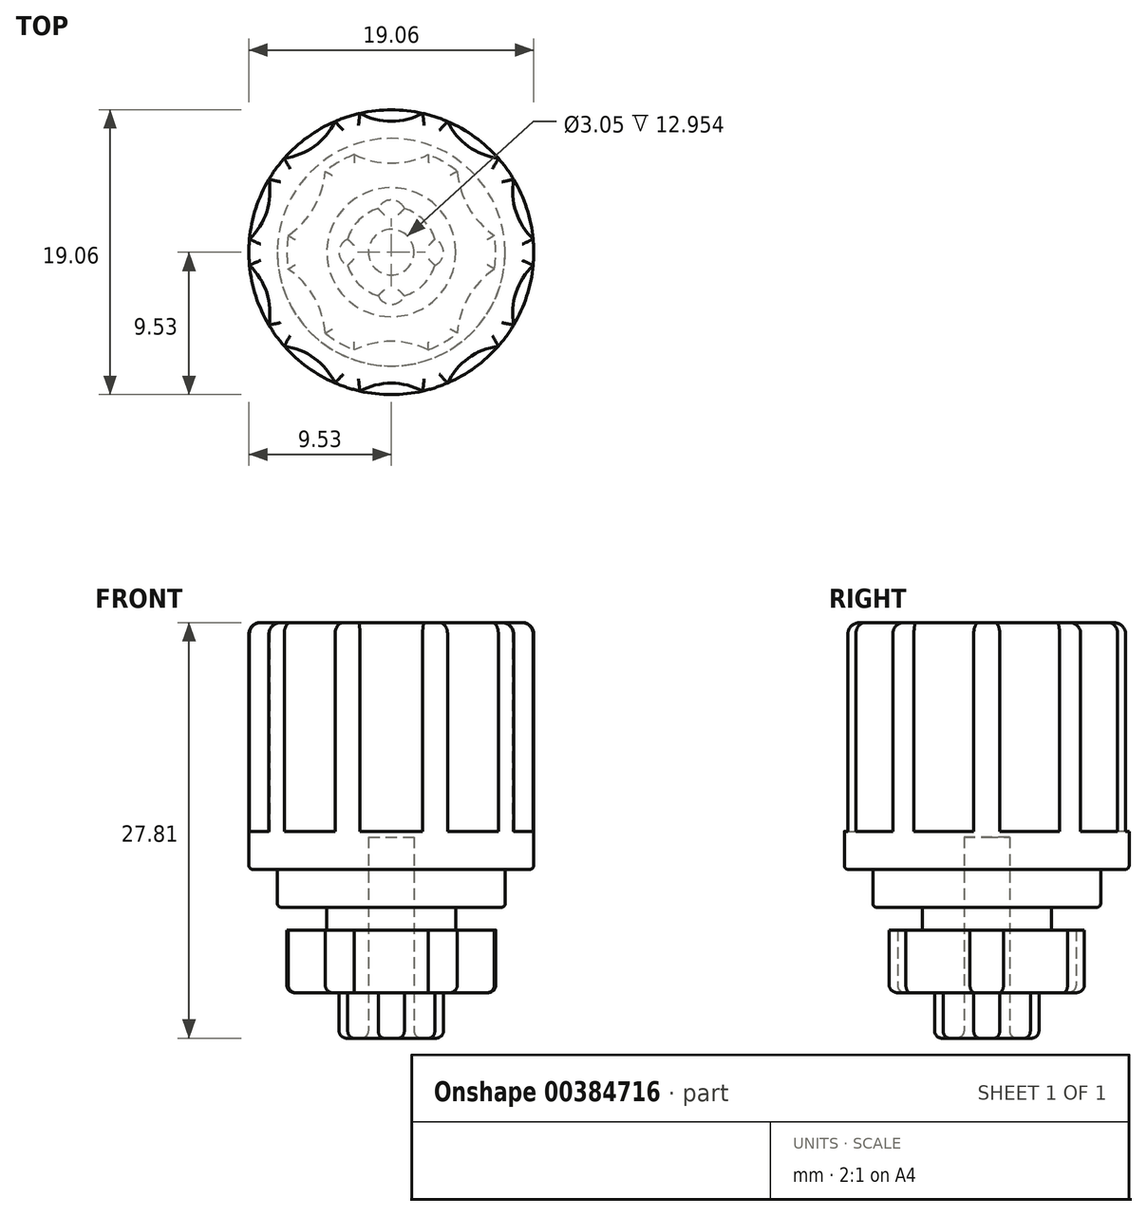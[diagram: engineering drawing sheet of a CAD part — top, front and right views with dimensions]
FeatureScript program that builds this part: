
annotation { "Feature Type Name" : "Feature", "Feature Type Description" : "" }
export const myFeature = defineFeature(function(context is Context, id is Id, definition is map)
    precondition{}
    {
        {
            var Q0;
            Q0=qCreatedBy(makeId("Top.planeOp"),FACE);
            var sketch = newSketch(context, id + "F0", { "sketchPlane" : qUnion([Q0])});
            skCircle(sketch, "E0", {"center": v(0, 0) * mm, "radius": 9.53 * mm});
            skSolve(sketch);
        }
        {
            var Q0;
            Q0=qSketchRegion(id+"F0",true);
            extrude(context, id + "F1", {"entities" : qUnion([Q0]), "depth" : 16.5 * mm});
        }
        {
            var Q0;
            Q0=makeQuery(id+"F1.opExtrude","CAP_FACE",FACE,{"disambiguationData":[OSD([sQuery(id+"F0.wireOp",EDGE,"E0")])],"isStart":false});
            var sketch = newSketch(context, id + "F2", { "sketchPlane" : qUnion([Q0])});
            skCircle(sketch, "E1", {"center": v(0, 13.2) * mm, "radius": 4.45 * mm});
            skCircle(sketch, "E2.1.0", {"center": v(-7.76, 10.69) * mm, "radius": 4.45 * mm});
            skCircle(sketch, "E2.2.0", {"center": v(-12.56, 4.08) * mm, "radius": 4.44 * mm});
            skCircle(sketch, "E2.3.0", {"center": v(-12.56, -4.08) * mm, "radius": 4.45 * mm});
            skCircle(sketch, "E2.4.0", {"center": v(-7.76, -10.69) * mm, "radius": 4.44 * mm});
            skCircle(sketch, "E2.5.0", {"center": v(0, -13.2) * mm, "radius": 4.44 * mm});
            skCircle(sketch, "E2.6.0", {"center": v(7.76, -10.69) * mm, "radius": 4.45 * mm});
            skCircle(sketch, "E2.7.0", {"center": v(12.56, -4.08) * mm, "radius": 4.45 * mm});
            skCircle(sketch, "E2.8.0", {"center": v(12.56, 4.08) * mm, "radius": 4.45 * mm});
            skCircle(sketch, "E2.9.0", {"center": v(7.76, 10.69) * mm, "radius": 4.45 * mm});
            skPoint(sketch, "E2.center", {"position": v(0, 0) * mm});
            skSolve(sketch);
        }
        {
            var Q0;
            Q0=qSketchRegion(id+"F2",true);
            extrude(context, id + "F3", {"entities" : qUnion([Q0]), "operationType" : NewBodyOperationType.REMOVE, "oppositeDirection" : true, "depth" : 13.97 * mm});
        }
        {
            var Q0;
            Q0=makeQuery(id+"F1.opExtrude","CAP_FACE",FACE,{"disambiguationData":[OSD([sQuery(id+"F0.wireOp",EDGE,"E0")])],"isStart":false});
            fillet(context, id + "F4", {"entities" : qUnion([Q0]), "radius" : 0.76 * mm, "tangentPropagation" : true, "allowEdgeOverflow" : false});
        }
        {
            var Q0;
            Q0=makeQuery(id+"F1.opExtrude","CAP_FACE",FACE,{"disambiguationData":[OSD([sQuery(id+"F0.wireOp",EDGE,"E0")])],"isStart":true});
            var sketch = newSketch(context, id + "F5", { "sketchPlane" : qUnion([Q0])});
            skCircle(sketch, "E3", {"center": v(0, 0) * mm, "radius": 6.99 * mm});
            skSolve(sketch);
        }
        {
            var Q0;
            Q0=qSketchRegion(id+"F5",true);
            extrude(context, id + "F6", {"entities" : qUnion([Q0]), "operationType" : NewBodyOperationType.ADD, "depth" : 8.25 * mm, "offsetDistance" : 25.4 * mm});
        }
        {
            var Q0;
            Q0=makeQuery(id+"F6.opExtrude","CAP_FACE",FACE,{"disambiguationData":[OSD([sQuery(id+"F5.wireOp",EDGE,"E3")])],"isStart":false});
            var sketch = newSketch(context, id + "F7", { "sketchPlane" : qUnion([Q0])});
            skCircle(sketch, "E4", {"center": v(0, 11.68) * mm, "radius": 5.72 * mm});
            skCircle(sketch, "E5.1.0", {"center": v(-10.12, 5.84) * mm, "radius": 5.72 * mm});
            skCircle(sketch, "E5.2.0", {"center": v(-10.12, -5.84) * mm, "radius": 5.72 * mm});
            skCircle(sketch, "E5.3.0", {"center": v(0, -11.68) * mm, "radius": 5.72 * mm});
            skCircle(sketch, "E5.4.0", {"center": v(10.12, -5.84) * mm, "radius": 5.72 * mm});
            skPoint(sketch, "E5.center", {"position": v(0, 0) * mm});
            skCircle(sketch, "E6.1.5.0", {"center": v(10.12, 5.84) * mm, "radius": 5.72 * mm});
            skSolve(sketch);
        }
        {
            var Q0;
            Q0=qSketchRegion(id+"F7",true);
            extrude(context, id + "F8", {"entities" : qUnion([Q0]), "operationType" : NewBodyOperationType.REMOVE, "oppositeDirection" : true, "depth" : 7.62 * mm});
        }
        {
            var Q0;
            Q0=makeQuery(id+"F8.boolean.opBoolean","MERGE",FACE,{"derivedFrom":[makeQuery(id+"F1.opExtrude","CAP_FACE",FACE,{"disambiguationData":[OSD([sQuery(id+"F0.wireOp",EDGE,"E0")])],"isStart":true}),makeQuery(id+"F8.opExtrude","CAP_FACE",FACE,{"disambiguationData":[OSD([sQuery(id+"F7.wireOp",EDGE,"E4")])],"isStart":false}),makeQuery(id+"F8.opExtrude","CAP_FACE",FACE,{"disambiguationData":[OSD([sQuery(id+"F7.wireOp",EDGE,"E5.1.0")])],"isStart":false}),makeQuery(id+"F8.opExtrude","CAP_FACE",FACE,{"disambiguationData":[OSD([sQuery(id+"F7.wireOp",EDGE,"E5.2.0")])],"isStart":false}),makeQuery(id+"F8.opExtrude","CAP_FACE",FACE,{"disambiguationData":[OSD([sQuery(id+"F7.wireOp",EDGE,"E5.3.0")])],"isStart":false}),makeQuery(id+"F8.opExtrude","CAP_FACE",FACE,{"disambiguationData":[OSD([sQuery(id+"F7.wireOp",EDGE,"E5.4.0")])],"isStart":false})]});
            var sketch = newSketch(context, id + "F9", { "sketchPlane" : qUnion([Q0])});
            skCircle(sketch, "E7", {"center": v(0, 0) * mm, "radius": 6.99 * mm});
            skCircle(sketch, "E8", {"center": v(0, 0) * mm, "radius": 4.32 * mm});
            skSolve(sketch);
        }
        {
            var Q0;
            Q0=qSketchRegion(id+"F9",true);
            extrude(context, id + "F10", {"entities" : qUnion([Q0]), "operationType" : NewBodyOperationType.REMOVE, "depth" : 4.06 * mm, "offsetDistance" : 25.4 * mm});
        }
        {
            var Q0;
            Q0=makeQuery(id+"F10.boolean.opBoolean","MERGE",FACE,{"derivedFrom":[makeQuery(id+"F1.opExtrude","CAP_FACE",FACE,{"disambiguationData":[OSD([sQuery(id+"F0.wireOp",EDGE,"E0")])],"isStart":true}),makeQuery(id+"F10.opExtrude","CAP_FACE",FACE,{"disambiguationData":[OSD([sQuery(id+"F9.wireOp",EDGE,"E7"),sQuery(id+"F9.wireOp",EDGE,"E8")])],"isStart":true})]});
            var sketch = newSketch(context, id + "F11", { "sketchPlane" : qUnion([Q0])});
            skCircle(sketch, "E9", {"center": v(0, 0) * mm, "radius": 7.62 * mm});
            skSolve(sketch);
        }
        {
            var Q0;
            Q0=qSketchRegion(id+"F11",true);
            extrude(context, id + "F12", {"entities" : qUnion([Q0]), "operationType" : NewBodyOperationType.ADD, "depth" : 2.54 * mm, "offsetDistance" : 25.4 * mm});
        }
        {
            var Q0;
            Q0=makeQuery(id+"F6.opExtrude","CAP_FACE",FACE,{"disambiguationData":[OSD([sQuery(id+"F5.wireOp",EDGE,"E3")])],"isStart":false});
            fillet(context, id + "F13", {"entities" : qUnion([Q0]), "radius" : 0.5 * mm, "tangentPropagation" : true, "allowEdgeOverflow" : false});
        }
        {
            var Q0;
            Q0=makeQuery(id+"F12.opExtrude","CAP_EDGE",EDGE,{"disambiguationData":[OSD([sQuery(id+"F11.wireOp",EDGE,"E9")])],"isStart":false});
            var Q1;
            Q1=makeQuery(id+"F1.opExtrude","CAP_EDGE",EDGE,{"disambiguationData":[OSD([sQuery(id+"F0.wireOp",EDGE,"E0")])],"isStart":true});
            var Q2;
            Q2=makeQuery(id+"F3.boolean.opBoolean","INTERSECT",EDGE,{"derivedFrom":[makeQuery(id+"F1.opExtrude","SWEPT_FACE",FACE,{"disambiguationData":[OSD([sQuery(id+"F0.wireOp",EDGE,"E0")])]}),makeQuery(id+"F3.opExtrude","CAP_FACE",FACE,{"disambiguationData":[OSD([sQuery(id+"F2.wireOp",EDGE,"cbdd18e0-91e5-42c7-8da3-7d40650399a5.4.0")])],"isStart":false})]});
            var Q3;
            Q3=makeQuery(id+"F3.boolean.opBoolean","INTERSECT",EDGE,{"derivedFrom":[makeQuery(id+"F1.opExtrude","SWEPT_FACE",FACE,{"disambiguationData":[OSD([sQuery(id+"F0.wireOp",EDGE,"E0")])]}),makeQuery(id+"F3.opExtrude","CAP_FACE",FACE,{"disambiguationData":[OSD([sQuery(id+"F2.wireOp",EDGE,"cbdd18e0-91e5-42c7-8da3-7d40650399a5.5.0")])],"isStart":false})]});
            var Q4;
            Q4=makeQuery(id+"F3.boolean.opBoolean","INTERSECT",EDGE,{"disambiguationData":[OD(0.0)],"derivedFrom":[makeQuery(id+"F1.opExtrude","SWEPT_FACE",FACE,{"disambiguationData":[OSD([sQuery(id+"F0.wireOp",EDGE,"E0")])]}),makeQuery(id+"F3.opExtrude","SWEPT_FACE",FACE,{"disambiguationData":[OSD([sQuery(id+"F2.wireOp",EDGE,"cbdd18e0-91e5-42c7-8da3-7d40650399a5.4.0")])]})]});
            var Q5;
            Q5=makeQuery(id+"F3.boolean.opBoolean","INTERSECT",EDGE,{"disambiguationData":[OD(1.0)],"derivedFrom":[makeQuery(id+"F1.opExtrude","SWEPT_FACE",FACE,{"disambiguationData":[OSD([sQuery(id+"F0.wireOp",EDGE,"E0")])]}),makeQuery(id+"F3.opExtrude","SWEPT_FACE",FACE,{"disambiguationData":[OSD([sQuery(id+"F2.wireOp",EDGE,"cbdd18e0-91e5-42c7-8da3-7d40650399a5.4.0")])]})]});
            var Q6;
            Q6=makeQuery(id+"F3.boolean.opBoolean","INTERSECT",EDGE,{"disambiguationData":[OD(0.0)],"derivedFrom":[makeQuery(id+"F1.opExtrude","SWEPT_FACE",FACE,{"disambiguationData":[OSD([sQuery(id+"F0.wireOp",EDGE,"E0")])]}),makeQuery(id+"F3.opExtrude","SWEPT_FACE",FACE,{"disambiguationData":[OSD([sQuery(id+"F2.wireOp",EDGE,"cbdd18e0-91e5-42c7-8da3-7d40650399a5.5.0")])]})]});
            var Q7;
            Q7=makeQuery(id+"F3.boolean.opBoolean","INTERSECT",EDGE,{"disambiguationData":[OD(1.0)],"derivedFrom":[makeQuery(id+"F1.opExtrude","SWEPT_FACE",FACE,{"disambiguationData":[OSD([sQuery(id+"F0.wireOp",EDGE,"E0")])]}),makeQuery(id+"F3.opExtrude","SWEPT_FACE",FACE,{"disambiguationData":[OSD([sQuery(id+"F2.wireOp",EDGE,"cbdd18e0-91e5-42c7-8da3-7d40650399a5.5.0")])]})]});
            var Q8;
            Q8=makeQuery(id+"F3.boolean.opBoolean","INTERSECT",EDGE,{"disambiguationData":[OD(0.0)],"derivedFrom":[makeQuery(id+"F1.opExtrude","SWEPT_FACE",FACE,{"disambiguationData":[OSD([sQuery(id+"F0.wireOp",EDGE,"E0")])]}),makeQuery(id+"F3.opExtrude","SWEPT_FACE",FACE,{"disambiguationData":[OSD([sQuery(id+"F2.wireOp",EDGE,"cbdd18e0-91e5-42c7-8da3-7d40650399a5.6.0")])]})]});
            var Q9;
            Q9=makeQuery(id+"F3.boolean.opBoolean","INTERSECT",EDGE,{"derivedFrom":[makeQuery(id+"F1.opExtrude","SWEPT_FACE",FACE,{"disambiguationData":[OSD([sQuery(id+"F0.wireOp",EDGE,"E0")])]}),makeQuery(id+"F3.opExtrude","CAP_FACE",FACE,{"disambiguationData":[OSD([sQuery(id+"F2.wireOp",EDGE,"cbdd18e0-91e5-42c7-8da3-7d40650399a5.6.0")])],"isStart":false})]});
            var Q10;
            Q10=makeQuery(id+"F3.boolean.opBoolean","INTERSECT",EDGE,{"disambiguationData":[OD(1.0)],"derivedFrom":[makeQuery(id+"F1.opExtrude","SWEPT_FACE",FACE,{"disambiguationData":[OSD([sQuery(id+"F0.wireOp",EDGE,"E0")])]}),makeQuery(id+"F3.opExtrude","SWEPT_FACE",FACE,{"disambiguationData":[OSD([sQuery(id+"F2.wireOp",EDGE,"cbdd18e0-91e5-42c7-8da3-7d40650399a5.6.0")])]})]});
            var Q11;
            Q11=makeQuery(id+"F3.boolean.opBoolean","INTERSECT",EDGE,{"disambiguationData":[OD(0.0)],"derivedFrom":[makeQuery(id+"F1.opExtrude","SWEPT_FACE",FACE,{"disambiguationData":[OSD([sQuery(id+"F0.wireOp",EDGE,"E0")])]}),makeQuery(id+"F3.opExtrude","SWEPT_FACE",FACE,{"disambiguationData":[OSD([sQuery(id+"F2.wireOp",EDGE,"cbdd18e0-91e5-42c7-8da3-7d40650399a5.7.0")])]})]});
            var Q12;
            Q12=makeQuery(id+"F3.boolean.opBoolean","INTERSECT",EDGE,{"derivedFrom":[makeQuery(id+"F1.opExtrude","SWEPT_FACE",FACE,{"disambiguationData":[OSD([sQuery(id+"F0.wireOp",EDGE,"E0")])]}),makeQuery(id+"F3.opExtrude","CAP_FACE",FACE,{"disambiguationData":[OSD([sQuery(id+"F2.wireOp",EDGE,"cbdd18e0-91e5-42c7-8da3-7d40650399a5.7.0")])],"isStart":false})]});
            var Q13;
            Q13=makeQuery(id+"F3.boolean.opBoolean","INTERSECT",EDGE,{"disambiguationData":[OD(1.0)],"derivedFrom":[makeQuery(id+"F1.opExtrude","SWEPT_FACE",FACE,{"disambiguationData":[OSD([sQuery(id+"F0.wireOp",EDGE,"E0")])]}),makeQuery(id+"F3.opExtrude","SWEPT_FACE",FACE,{"disambiguationData":[OSD([sQuery(id+"F2.wireOp",EDGE,"cbdd18e0-91e5-42c7-8da3-7d40650399a5.7.0")])]})]});
            var Q14;
            Q14=makeQuery(id+"F3.boolean.opBoolean","INTERSECT",EDGE,{"derivedFrom":[makeQuery(id+"F1.opExtrude","SWEPT_FACE",FACE,{"disambiguationData":[OSD([sQuery(id+"F0.wireOp",EDGE,"E0")])]}),makeQuery(id+"F3.opExtrude","CAP_FACE",FACE,{"disambiguationData":[OSD([sQuery(id+"F2.wireOp",EDGE,"cbdd18e0-91e5-42c7-8da3-7d40650399a5.8.0")])],"isStart":false})]});
            var Q15;
            Q15=makeQuery(id+"F3.boolean.opBoolean","INTERSECT",EDGE,{"disambiguationData":[OD(0.0)],"derivedFrom":[makeQuery(id+"F1.opExtrude","SWEPT_FACE",FACE,{"disambiguationData":[OSD([sQuery(id+"F0.wireOp",EDGE,"E0")])]}),makeQuery(id+"F3.opExtrude","SWEPT_FACE",FACE,{"disambiguationData":[OSD([sQuery(id+"F2.wireOp",EDGE,"cbdd18e0-91e5-42c7-8da3-7d40650399a5.8.0")])]})]});
            var Q16;
            Q16=makeQuery(id+"F3.boolean.opBoolean","INTERSECT",EDGE,{"disambiguationData":[OD(1.0)],"derivedFrom":[makeQuery(id+"F1.opExtrude","SWEPT_FACE",FACE,{"disambiguationData":[OSD([sQuery(id+"F0.wireOp",EDGE,"E0")])]}),makeQuery(id+"F3.opExtrude","SWEPT_FACE",FACE,{"disambiguationData":[OSD([sQuery(id+"F2.wireOp",EDGE,"cbdd18e0-91e5-42c7-8da3-7d40650399a5.8.0")])]})]});
            var Q17;
            Q17=makeQuery(id+"F3.boolean.opBoolean","INTERSECT",EDGE,{"disambiguationData":[OD(1.0)],"derivedFrom":[makeQuery(id+"F1.opExtrude","SWEPT_FACE",FACE,{"disambiguationData":[OSD([sQuery(id+"F0.wireOp",EDGE,"E0")])]}),makeQuery(id+"F3.opExtrude","SWEPT_FACE",FACE,{"disambiguationData":[OSD([sQuery(id+"F2.wireOp",EDGE,"cbdd18e0-91e5-42c7-8da3-7d40650399a5.9.0")])]})]});
            var Q18;
            Q18=makeQuery(id+"F3.boolean.opBoolean","INTERSECT",EDGE,{"derivedFrom":[makeQuery(id+"F1.opExtrude","SWEPT_FACE",FACE,{"disambiguationData":[OSD([sQuery(id+"F0.wireOp",EDGE,"E0")])]}),makeQuery(id+"F3.opExtrude","CAP_FACE",FACE,{"disambiguationData":[OSD([sQuery(id+"F2.wireOp",EDGE,"cbdd18e0-91e5-42c7-8da3-7d40650399a5.9.0")])],"isStart":false})]});
            var Q19;
            Q19=makeQuery(id+"F3.boolean.opBoolean","INTERSECT",EDGE,{"disambiguationData":[OD(0.0)],"derivedFrom":[makeQuery(id+"F1.opExtrude","SWEPT_FACE",FACE,{"disambiguationData":[OSD([sQuery(id+"F0.wireOp",EDGE,"E0")])]}),makeQuery(id+"F3.opExtrude","SWEPT_FACE",FACE,{"disambiguationData":[OSD([sQuery(id+"F2.wireOp",EDGE,"cbdd18e0-91e5-42c7-8da3-7d40650399a5.9.0")])]})]});
            var Q20;
            Q20=makeQuery(id+"F3.boolean.opBoolean","INTERSECT",EDGE,{"disambiguationData":[OD(1.0)],"derivedFrom":[makeQuery(id+"F1.opExtrude","SWEPT_FACE",FACE,{"disambiguationData":[OSD([sQuery(id+"F0.wireOp",EDGE,"E0")])]}),makeQuery(id+"F3.opExtrude","SWEPT_FACE",FACE,{"disambiguationData":[OSD([sQuery(id+"F2.wireOp",EDGE,"x1HnmwHp-epZq-sPKC-iZKM-3ESXbZE1iOWw")])]})]});
            var Q21;
            Q21=makeQuery(id+"F3.boolean.opBoolean","INTERSECT",EDGE,{"derivedFrom":[makeQuery(id+"F1.opExtrude","SWEPT_FACE",FACE,{"disambiguationData":[OSD([sQuery(id+"F0.wireOp",EDGE,"E0")])]}),makeQuery(id+"F3.opExtrude","CAP_FACE",FACE,{"disambiguationData":[OSD([sQuery(id+"F2.wireOp",EDGE,"x1HnmwHp-epZq-sPKC-iZKM-3ESXbZE1iOWw")])],"isStart":false})]});
            var Q22;
            Q22=makeQuery(id+"F3.boolean.opBoolean","INTERSECT",EDGE,{"disambiguationData":[OD(0.0)],"derivedFrom":[makeQuery(id+"F1.opExtrude","SWEPT_FACE",FACE,{"disambiguationData":[OSD([sQuery(id+"F0.wireOp",EDGE,"E0")])]}),makeQuery(id+"F3.opExtrude","SWEPT_FACE",FACE,{"disambiguationData":[OSD([sQuery(id+"F2.wireOp",EDGE,"x1HnmwHp-epZq-sPKC-iZKM-3ESXbZE1iOWw")])]})]});
            var Q23;
            Q23=makeQuery(id+"F3.boolean.opBoolean","INTERSECT",EDGE,{"derivedFrom":[makeQuery(id+"F1.opExtrude","SWEPT_FACE",FACE,{"disambiguationData":[OSD([sQuery(id+"F0.wireOp",EDGE,"E0")])]}),makeQuery(id+"F3.opExtrude","CAP_FACE",FACE,{"disambiguationData":[OSD([sQuery(id+"F2.wireOp",EDGE,"cbdd18e0-91e5-42c7-8da3-7d40650399a5.1.0")])],"isStart":false})]});
            var Q24;
            Q24=makeQuery(id+"F3.boolean.opBoolean","INTERSECT",EDGE,{"disambiguationData":[OD(1.0)],"derivedFrom":[makeQuery(id+"F1.opExtrude","SWEPT_FACE",FACE,{"disambiguationData":[OSD([sQuery(id+"F0.wireOp",EDGE,"E0")])]}),makeQuery(id+"F3.opExtrude","SWEPT_FACE",FACE,{"disambiguationData":[OSD([sQuery(id+"F2.wireOp",EDGE,"cbdd18e0-91e5-42c7-8da3-7d40650399a5.1.0")])]})]});
            var Q25;
            Q25=makeQuery(id+"F3.boolean.opBoolean","INTERSECT",EDGE,{"disambiguationData":[OD(0.0)],"derivedFrom":[makeQuery(id+"F1.opExtrude","SWEPT_FACE",FACE,{"disambiguationData":[OSD([sQuery(id+"F0.wireOp",EDGE,"E0")])]}),makeQuery(id+"F3.opExtrude","SWEPT_FACE",FACE,{"disambiguationData":[OSD([sQuery(id+"F2.wireOp",EDGE,"cbdd18e0-91e5-42c7-8da3-7d40650399a5.1.0")])]})]});
            var Q26;
            Q26=makeQuery(id+"F3.boolean.opBoolean","INTERSECT",EDGE,{"disambiguationData":[OD(1.0)],"derivedFrom":[makeQuery(id+"F1.opExtrude","SWEPT_FACE",FACE,{"disambiguationData":[OSD([sQuery(id+"F0.wireOp",EDGE,"E0")])]}),makeQuery(id+"F3.opExtrude","SWEPT_FACE",FACE,{"disambiguationData":[OSD([sQuery(id+"F2.wireOp",EDGE,"cbdd18e0-91e5-42c7-8da3-7d40650399a5.2.0")])]})]});
            var Q27;
            Q27=makeQuery(id+"F3.boolean.opBoolean","INTERSECT",EDGE,{"derivedFrom":[makeQuery(id+"F1.opExtrude","SWEPT_FACE",FACE,{"disambiguationData":[OSD([sQuery(id+"F0.wireOp",EDGE,"E0")])]}),makeQuery(id+"F3.opExtrude","CAP_FACE",FACE,{"disambiguationData":[OSD([sQuery(id+"F2.wireOp",EDGE,"cbdd18e0-91e5-42c7-8da3-7d40650399a5.2.0")])],"isStart":false})]});
            var Q28;
            Q28=makeQuery(id+"F3.boolean.opBoolean","INTERSECT",EDGE,{"disambiguationData":[OD(0.0)],"derivedFrom":[makeQuery(id+"F1.opExtrude","SWEPT_FACE",FACE,{"disambiguationData":[OSD([sQuery(id+"F0.wireOp",EDGE,"E0")])]}),makeQuery(id+"F3.opExtrude","SWEPT_FACE",FACE,{"disambiguationData":[OSD([sQuery(id+"F2.wireOp",EDGE,"cbdd18e0-91e5-42c7-8da3-7d40650399a5.2.0")])]})]});
            var Q29;
            Q29=makeQuery(id+"F3.boolean.opBoolean","INTERSECT",EDGE,{"disambiguationData":[OD(1.0)],"derivedFrom":[makeQuery(id+"F1.opExtrude","SWEPT_FACE",FACE,{"disambiguationData":[OSD([sQuery(id+"F0.wireOp",EDGE,"E0")])]}),makeQuery(id+"F3.opExtrude","SWEPT_FACE",FACE,{"disambiguationData":[OSD([sQuery(id+"F2.wireOp",EDGE,"cbdd18e0-91e5-42c7-8da3-7d40650399a5.3.0")])]})]});
            var Q30;
            Q30=makeQuery(id+"F3.boolean.opBoolean","INTERSECT",EDGE,{"derivedFrom":[makeQuery(id+"F1.opExtrude","SWEPT_FACE",FACE,{"disambiguationData":[OSD([sQuery(id+"F0.wireOp",EDGE,"E0")])]}),makeQuery(id+"F3.opExtrude","CAP_FACE",FACE,{"disambiguationData":[OSD([sQuery(id+"F2.wireOp",EDGE,"cbdd18e0-91e5-42c7-8da3-7d40650399a5.3.0")])],"isStart":false})]});
            var Q31;
            Q31=makeQuery(id+"F3.boolean.opBoolean","INTERSECT",EDGE,{"disambiguationData":[OD(0.0)],"derivedFrom":[makeQuery(id+"F1.opExtrude","SWEPT_FACE",FACE,{"disambiguationData":[OSD([sQuery(id+"F0.wireOp",EDGE,"E0")])]}),makeQuery(id+"F3.opExtrude","SWEPT_FACE",FACE,{"disambiguationData":[OSD([sQuery(id+"F2.wireOp",EDGE,"cbdd18e0-91e5-42c7-8da3-7d40650399a5.3.0")])]})]});
            fillet(context, id + "F14", {"entities" : qUnion([Q0, Q1, Q2, Q3, Q4, Q5, Q6, Q7, Q8, Q9, Q10, Q11, Q12, Q13, Q14, Q15, Q16, Q17, Q18, Q19, Q20, Q21, Q22, Q23, Q24, Q25, Q26, Q27, Q28, Q29, Q30, Q31]), "radius" : 0.25 * mm, "tangentPropagation" : true, "allowEdgeOverflow" : false});
        }
        {
            var Q0;
            Q0=makeQuery(id+"F6.opExtrude","CAP_FACE",FACE,{"disambiguationData":[OSD([sQuery(id+"F5.wireOp",EDGE,"E3")])],"isStart":false});
            var sketch = newSketch(context, id + "F15", { "sketchPlane" : qUnion([Q0])});
            skCircle(sketch, "E10", {"center": v(0, 0) * mm, "radius": 1.52 * mm});
            skSolve(sketch);
        }
        {
            var Q0;
            Q0=qSketchRegion(id+"F15",true);
            extrude(context, id + "F16", {"entities" : qUnion([Q0]), "operationType" : NewBodyOperationType.REMOVE, "oppositeDirection" : true, "depth" : 10.4 * mm, "offsetDistance" : 25.4 * mm});
        }
        {
            var Q0;
            Q0=makeQuery(id+"F6.opExtrude","CAP_FACE",FACE,{"disambiguationData":[OSD([sQuery(id+"F5.wireOp",EDGE,"E3")])],"isStart":false});
            var sketch = newSketch(context, id + "F17", { "sketchPlane" : qUnion([Q0])});
            skArc(sketch, "E11", {"start": v(0.87, -2.92) * mm, "mid": v(0, 3.05) * mm, "end": v(-0.87, -2.92) * mm});
            skArc(sketch, "E12", {"start": v(-0.87, -2.92) * mm, "mid": v(0, -3.5) * mm, "end": v(0.87, -2.92) * mm});
            skCircle(sketch, "E13", {"center": v(0, 0) * mm, "radius": 1.52 * mm});
            skArc(sketch, "E14.1.0", {"start": v(2.92, -0.87) * mm, "mid": v(3.5, 0) * mm, "end": v(2.92, 0.87) * mm});
            skArc(sketch, "E15.2.2.0", {"start": v(0.87, 2.92) * mm, "mid": v(0, 3.5) * mm, "end": v(-0.87, 2.92) * mm});
            skArc(sketch, "E15.2.3.0", {"start": v(-2.92, 0.87) * mm, "mid": v(-3.5, 0) * mm, "end": v(-2.92, -0.87) * mm});
            skSolve(sketch);
        }
        {
            var Q0;
            Q0=qSketchRegion(id+"F17",true);
            extrude(context, id + "F18", {"entities" : qUnion([Q0]), "operationType" : NewBodyOperationType.ADD, "depth" : 3.05 * mm, "offsetDistance" : 25.4 * mm});
        }
        {
            var Q0;
            Q0=makeQuery(id+"F18.opExtrude","CAP_FACE",FACE,{"disambiguationData":[OSD([sQuery(id+"F17.wireOp",EDGE,"E11"),sQuery(id+"F17.wireOp",EDGE,"E12"),sQuery(id+"F17.wireOp",EDGE,"E13")])],"isStart":false});
            fillet(context, id + "F19", {"entities" : qUnion([Q0]), "radius" : 0.5 * mm, "tangentPropagation" : true, "allowEdgeOverflow" : false});
        }
    });
